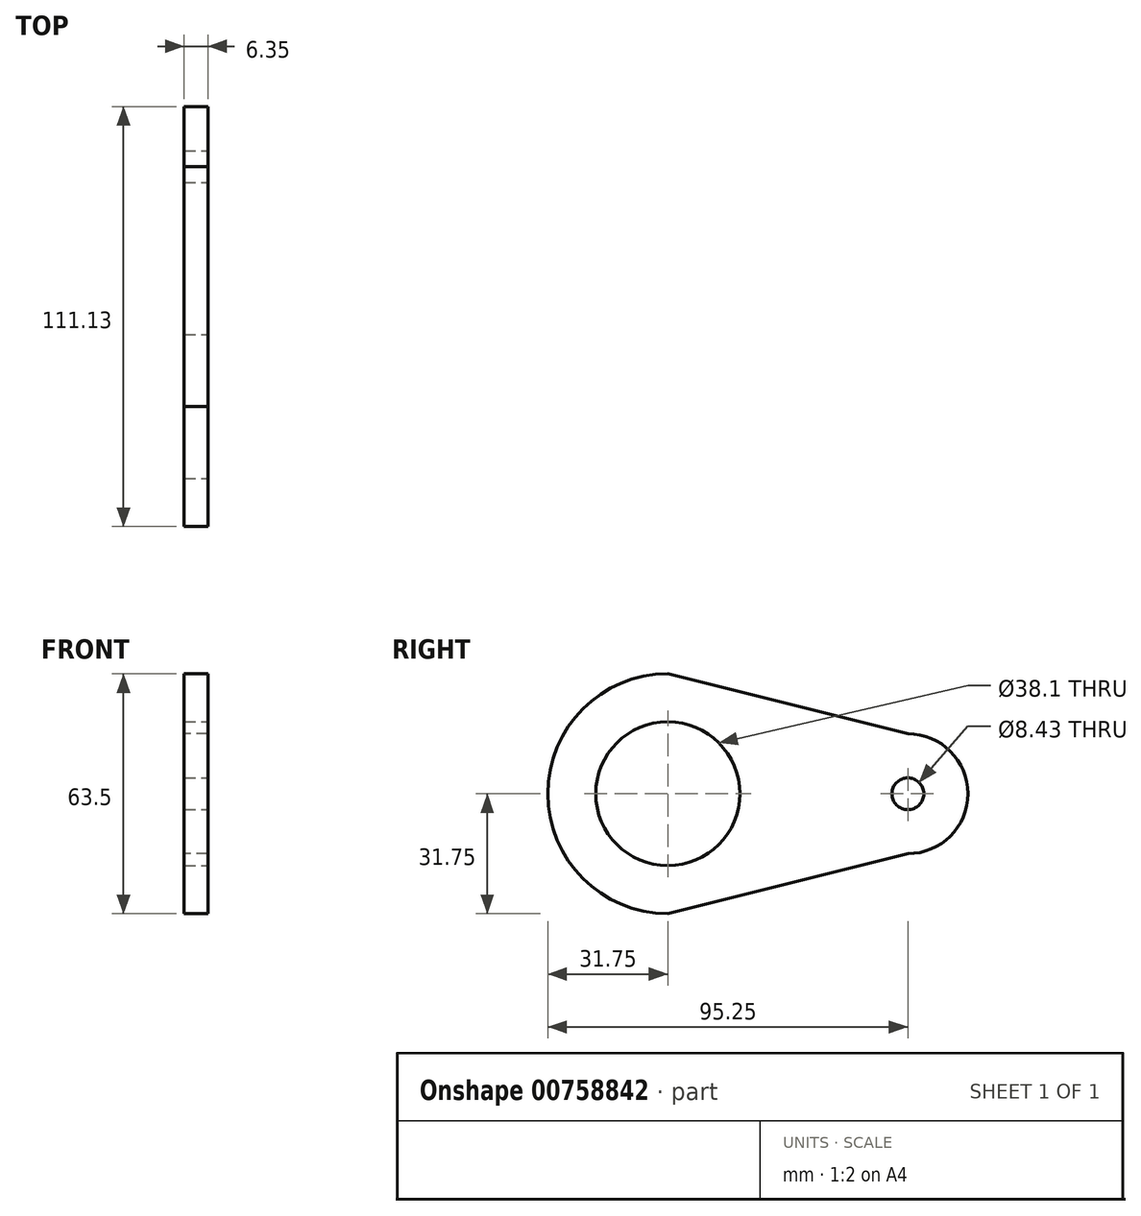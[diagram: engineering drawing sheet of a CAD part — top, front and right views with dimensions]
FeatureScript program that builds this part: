
annotation { "Feature Type Name" : "Feature", "Feature Type Description" : "" }
export const myFeature = defineFeature(function(context is Context, id is Id, definition is map)
    precondition{}
    {
        {
            var Q0;
            Q0=qCreatedBy(makeId("Right.planeOp"),FACE);
            var sketch = newSketch(context, id + "F0", { "sketchPlane" : qUnion([Q0])});
            skArc(sketch, "E0", {"start": v(0, 31.75) * mm, "mid": v(-31.75, 0) * mm, "end": v(0, -31.75) * mm});
            skArc(sketch, "E1", {"start": v(63.5, -15.88) * mm, "mid": v(79.38, 0) * mm, "end": v(63.5, 15.87) * mm});
            skLineSegment(sketch, "E2", {"start": v(0, 31.75) * mm, "end": v(63.5, 15.88) * mm});
            skLineSegment(sketch, "E3", {"start": v(0, -31.75) * mm, "end": v(63.5, -15.88) * mm});
            skSolve(sketch);
        }
        {
            var Q0;
            Q0=makeQuery(id+"F0.imprint","IMPRINT",FACE,{"disambiguationData":[TD([[makeQuery(id+"F0.imprint","IMPRINT",EDGE,{"derivedFrom":sQuery(id+"F0.wireOp",EDGE,"E0")}),1.0]])]});
            extrude(context, id + "F1", {"entities" : qUnion([Q0]), "depth" : 6.35 * mm, "offsetDistance" : 25.4 * mm});
        }
        {
            var Q0;
            Q0=makeQuery(id+"F1.opExtrude","CAP_FACE",FACE,{"disambiguationData":[OSD([sQuery(id+"F0.wireOp",EDGE,"E0"),sQuery(id+"F0.wireOp",EDGE,"E1"),sQuery(id+"F0.wireOp",EDGE,"E2"),sQuery(id+"F0.wireOp",EDGE,"E3")])],"isStart":false});
            var sketch = newSketch(context, id + "F2", { "sketchPlane" : qUnion([Q0])});
            skPoint(sketch, "E4", {"position": v(0, 0) * mm});
            skPoint(sketch, "E5", {"position": v(63.5, 0) * mm});
            skSolve(sketch);
        }
        {
            var Q0;
            Q0=sQuery(id+"F2.wireOp",VERTEX,"E4");
            var Q1;
            Q1=makeQuery(id+"F1.opExtrude","SWEPT_BODY",BODY,{"disambiguationData":[OSD([sQuery(id+"F0.wireOp",EDGE,"E0"),sQuery(id+"F0.wireOp",EDGE,"E1"),sQuery(id+"F0.wireOp",EDGE,"E2"),sQuery(id+"F0.wireOp",EDGE,"E3")])]});
            hole(context, id + "F3", {"style" : HoleStyle.SIMPLE, "endStyle" : HoleEndStyle.BLIND, "holeDiameter" : 38.1 * mm, "majorDiameter" : 6.35 * mm, "holeDepth" : 6.35 * mm, "isTappedThrough" : true, "tappedDepth" : 12.7 * mm, "tapClearance" : 3, "startFromSketch" : true, "locations" : qUnion([Q0]), "scope" : qUnion([Q1])});
        }
        {
            var Q0;
            Q0=sQuery(id+"F2.wireOp",VERTEX,"E5");
            var Q1;
            Q1=makeQuery(id+"F1.opExtrude","SWEPT_BODY",BODY,{"disambiguationData":[OSD([sQuery(id+"F0.wireOp",EDGE,"E0"),sQuery(id+"F0.wireOp",EDGE,"E1"),sQuery(id+"F0.wireOp",EDGE,"E2"),sQuery(id+"F0.wireOp",EDGE,"E3")])]});
            hole(context, id + "F4", {"style" : HoleStyle.SIMPLE, "endStyle" : HoleEndStyle.THROUGH, "standardTappedOrClearance" : lookupTablePath({ "standard" : "ANSI", "engagement" : "75%", "pitch" : "24 tpi", "size" : "3/8", "type" : "Tapped" }), "standardBlindInLast" : lookupTablePath({ "standard" : "ANSI", "engagement" : "75%", "pitch" : "24 tpi", "size" : "3/8", "type" : "Tapped" }), "holeDiameter" : 8.43 * mm, "majorDiameter" : 9.52 * mm, "showTappedDepth" : true, "isTappedThrough" : true, "tappedDepth" : 12.7 * mm, "tapClearance" : 3, "startFromSketch" : true, "locations" : qUnion([Q0]), "scope" : qUnion([Q1])});
        }
    });
